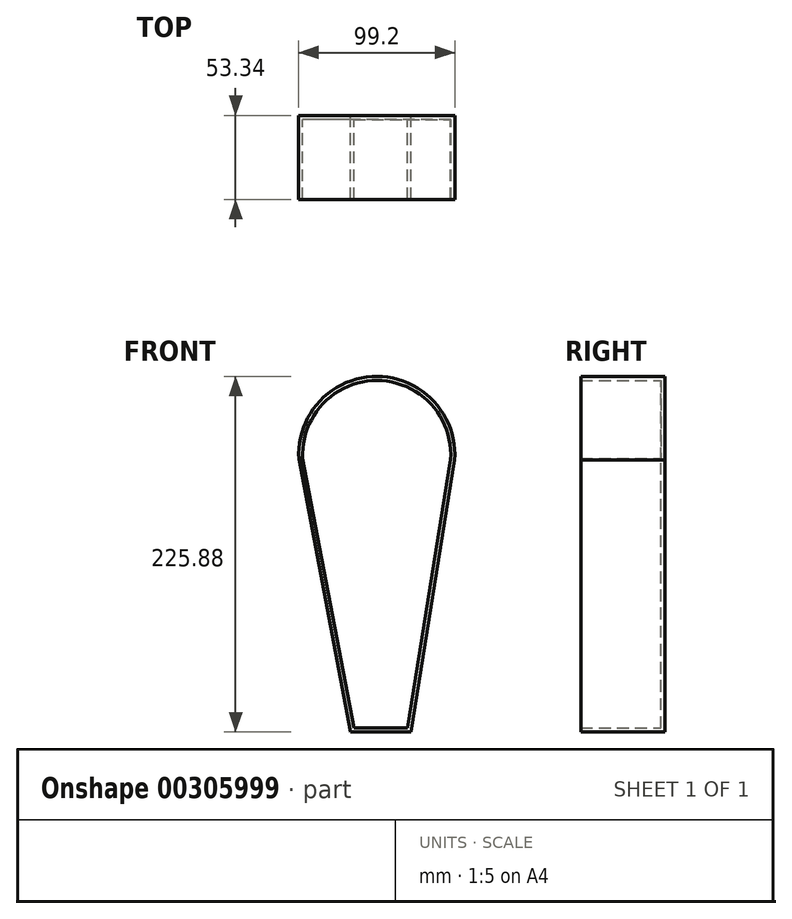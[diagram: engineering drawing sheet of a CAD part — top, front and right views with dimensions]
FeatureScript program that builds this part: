
annotation { "Feature Type Name" : "Feature", "Feature Type Description" : "" }
export const myFeature = defineFeature(function(context is Context, id is Id, definition is map)
    precondition{}
    {
        {
            var Q0;
            Q0=qCreatedBy(makeId("Front.planeOp"),FACE);
            var sketch = newSketch(context, id + "F0", { "sketchPlane" : qUnion([Q0])});
            skLineSegment(sketch, "E0", {"start": v(-16.35, -127.44) * mm, "end": v(22.01, -127.44) * mm});
            skLineSegment(sketch, "E1", {"start": v(22.01, -127.44) * mm, "end": v(49.83, 45.44) * mm});
            skLineSegment(sketch, "E2", {"start": v(2.83, -127.44) * mm, "end": v(2.83, 52.66) * mm, "construction": true});
            skLineSegment(sketch, "E3", {"start": v(-16.35, -127.44) * mm, "end": v(-49.17, 45.97) * mm});
            skArc(sketch, "E4", {"start": v(49.83, 45.44) * mm, "mid": v(0.61, 98.43) * mm, "end": v(-49.17, 45.97) * mm});
            skSolve(sketch);
        }
        {
            var Q0;
            Q0 = qSketchRegion(id + "F0", true);
            extrude(context, id + "F1", {"entities" : qUnion([Q0]), "depth" : 53.34 * mm});
        }
        {
            var Q0;
            Q0=makeQuery(id+"F1.opExtrude","CAP_FACE",FACE,{"disambiguationData":[OSD([sQuery(id+"F0.wireOp",EDGE,"E0"),sQuery(id+"F0.wireOp",EDGE,"E1"),sQuery(id+"F0.wireOp",EDGE,"E3"),sQuery(id+"F0.wireOp",EDGE,"E4")])],"isStart":false});
            shell(context, id + "F2", {"entities" : qUnion([Q0]), "thickness" : 2.54 * mm});
        }
    });
